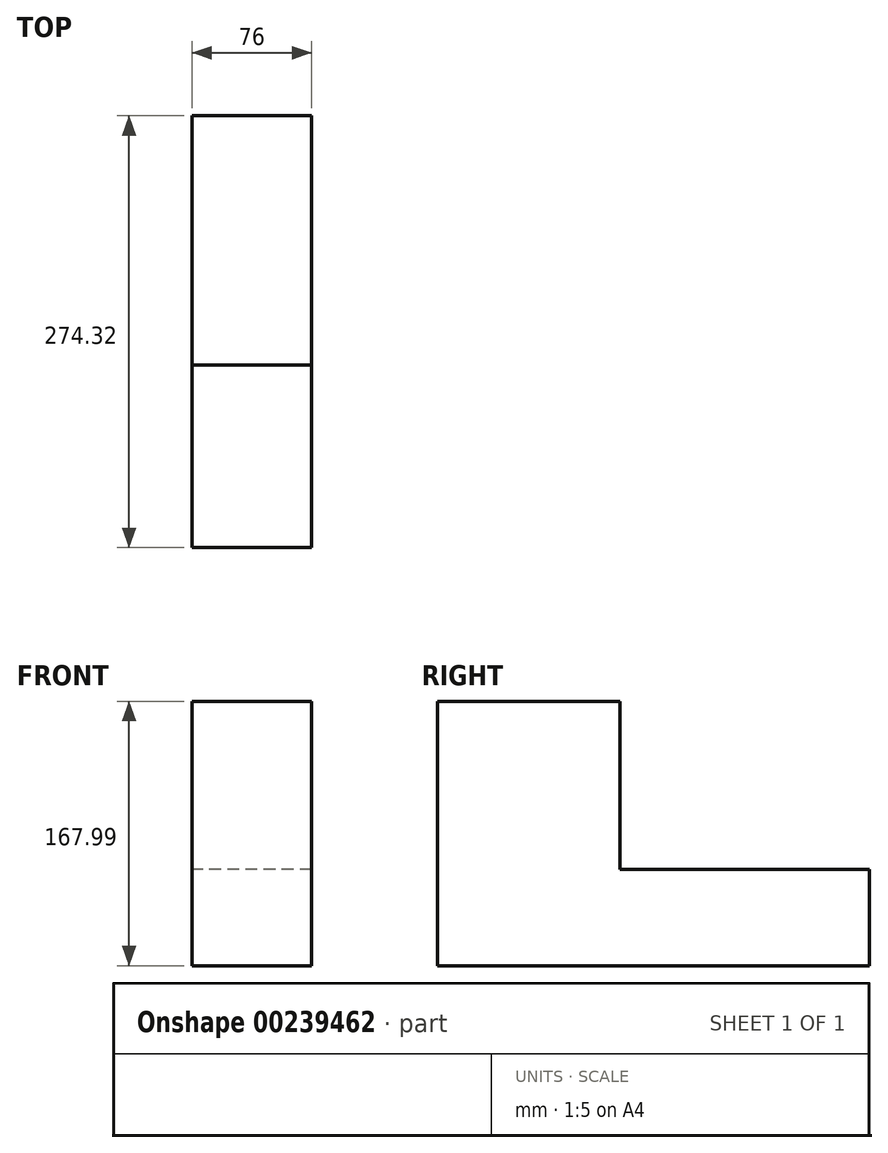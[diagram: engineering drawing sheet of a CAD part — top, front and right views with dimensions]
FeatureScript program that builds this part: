
annotation { "Feature Type Name" : "Feature", "Feature Type Description" : "" }
export const myFeature = defineFeature(function(context is Context, id is Id, definition is map)
    precondition{}
    {
        {
            var Q0;
            Q0=qCreatedBy(makeId("Front.planeOp"),FACE);
            var sketch = newSketch(context, id + "F0", { "sketchPlane" : qUnion([Q0])});
            skLineSegment(sketch, "E0.bottom", {"start": v(38, 14.78) * mm, "end": v(-38, 14.78) * mm});
            skLineSegment(sketch, "E0.top", {"start": v(38, -14.78) * mm, "end": v(-38, -14.78) * mm});
            skLineSegment(sketch, "E0.left", {"start": v(38, 14.78) * mm, "end": v(38, -14.78) * mm});
            skLineSegment(sketch, "E0.right", {"start": v(-38, 14.78) * mm, "end": v(-38, -14.78) * mm});
            skPoint(sketch, "E0.middle", {"position": v(0, 0) * mm});
            skSolve(sketch);
        }
        {
            var Q0;
            Q0=makeQuery(id+"F0.imprint","IMPRINT",FACE,{"disambiguationData":[TD([[makeQuery(id+"F0.imprint","IMPRINT",EDGE,{"derivedFrom":sQuery(id+"F0.wireOp",EDGE,"E0.bottom")}),1.0]])]});
            extrude(context, id + "F1", {"entities" : qUnion([Q0]), "endBound" : BoundingType.SYMMETRIC, "depth" : 274.32 * mm});
        }
        {
            var Q0;
            Q0=makeQuery(id+"F1.opExtrude","SWEPT_FACE",FACE,{"disambiguationData":[OSD([sQuery(id+"F0.wireOp",EDGE,"E0.bottom")])]});
            var sketch = newSketch(context, id + "F2", { "sketchPlane" : qUnion([Q0])});
            skLineSegment(sketch, "E1.bottom", {"start": v(-38, -137.16) * mm, "end": v(38, -137.16) * mm});
            skLineSegment(sketch, "E1.top", {"start": v(-38, -21.2) * mm, "end": v(38, -21.2) * mm});
            skLineSegment(sketch, "E1.left", {"start": v(-38, -137.16) * mm, "end": v(-38, -21.2) * mm});
            skLineSegment(sketch, "E1.right", {"start": v(38, -137.16) * mm, "end": v(38, -21.2) * mm});
            skSolve(sketch);
        }
        {
            var Q0;
            Q0 = qSketchRegion(id + "F2", true);
            extrude(context, id + "F3", {"entities" : qUnion([Q0]), "operationType" : NewBodyOperationType.ADD, "depth" : 138.43 * mm});
        }
        {
            var Q0;
            Q0=makeQuery(id+"F1.opExtrude","SWEPT_FACE",FACE,{"disambiguationData":[OSD([sQuery(id+"F0.wireOp",EDGE,"E0.bottom")])]});
            var sketch = newSketch(context, id + "F4", { "sketchPlane" : qUnion([Q0])});
            skLineSegment(sketch, "E2.bottom", {"start": v(-38, 137.16) * mm, "end": v(38, 137.16) * mm});
            skLineSegment(sketch, "E2.top", {"start": v(-38, -21.2) * mm, "end": v(38, -21.2) * mm});
            skLineSegment(sketch, "E2.left", {"start": v(-38, 137.16) * mm, "end": v(-38, -21.2) * mm});
            skLineSegment(sketch, "E2.right", {"start": v(38, 137.16) * mm, "end": v(38, -21.2) * mm});
            skSolve(sketch);
        }
        {
            var Q0;
            Q0 = qSketchRegion(id + "F4", true);
            extrude(context, id + "F5", {"entities" : qUnion([Q0]), "operationType" : NewBodyOperationType.ADD, "depth" : 31.5 * mm});
        }
    });
